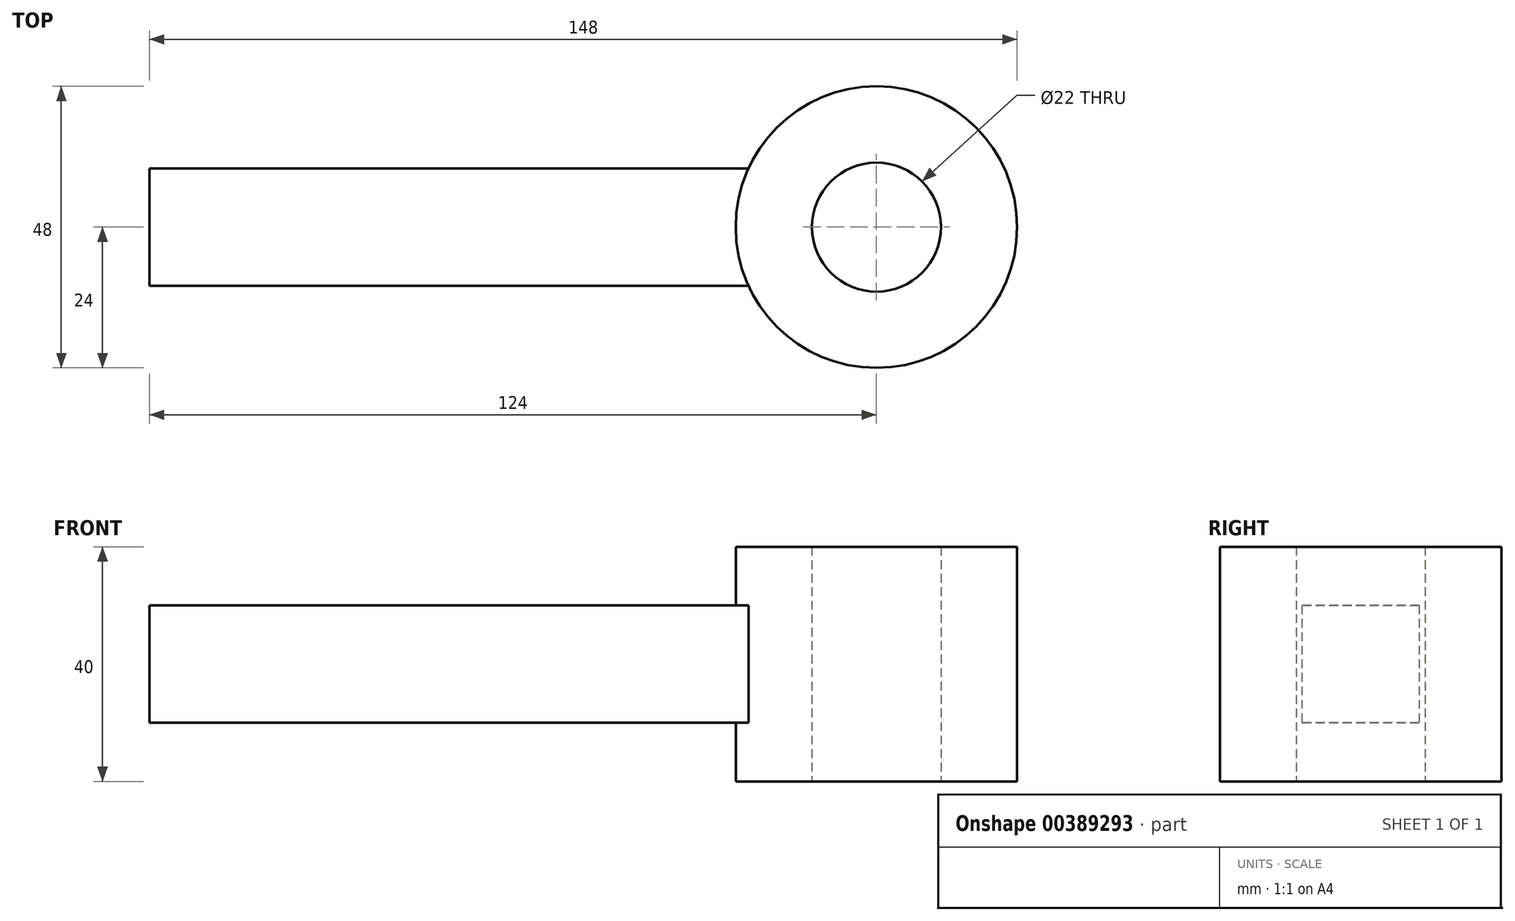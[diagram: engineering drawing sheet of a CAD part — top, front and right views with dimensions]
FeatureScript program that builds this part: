
annotation { "Feature Type Name" : "Feature", "Feature Type Description" : "" }
export const myFeature = defineFeature(function(context is Context, id is Id, definition is map)
    precondition{}
    {
        {
            var Q0;
            Q0=qCreatedBy(makeId("Top.planeOp"),FACE);
            var sketch = newSketch(context, id + "F0", { "sketchPlane" : qUnion([Q0])});
            skCircle(sketch, "E0", {"center": v(0, 0) * mm, "radius": 24 * mm});
            skLineSegment(sketch, "E1", {"start": v(-124, 0) * mm, "end": v(-124, -10) * mm});
            skLineSegment(sketch, "E2", {"start": v(-124, 0) * mm, "end": v(-124, 10) * mm});
            skLineSegment(sketch, "E3", {"start": v(-124, 10) * mm, "end": v(-21.82, 10) * mm});
            skLineSegment(sketch, "E4", {"start": v(-124, -10) * mm, "end": v(-21.82, -10) * mm});
            skCircle(sketch, "E5", {"center": v(0, 0) * mm, "radius": 11 * mm});
            skSolve(sketch);
        }
        {
            var Q0;
            {var subQ0=sQuery(id+"F0.wireOp",EDGE,"E0");var subQ1=makeQuery(id+"F0.imprint","INTERSECT",VERTEX,{"derivedFrom":[subQ0,sQuery(id+"F0.wireOp",EDGE,"E3")]});Q0=makeQuery(id+"F0.imprint","IMPRINT",FACE,{"disambiguationData":[TD([[makeQuery(id+"F0.imprint","IMPRINT",EDGE,{"disambiguationData":[TD([[subQ1,-1.0]])],"derivedFrom":subQ0}),1.0]])]});}
            extrude(context, id + "F1", {"entities" : qUnion([Q0]), "endBound" : BoundingType.SYMMETRIC, "depth" : 40 * mm});
        }
        {
            var Q0;
            Q0=makeQuery(id+"F0.imprint","IMPRINT",FACE,{"disambiguationData":[TD([[makeQuery(id+"F0.imprint","IMPRINT",EDGE,{"derivedFrom":sQuery(id+"F0.wireOp",EDGE,"E1")}),1.0]])]});
            extrude(context, id + "F2", {"entities" : qUnion([Q0]), "operationType" : NewBodyOperationType.ADD, "endBound" : BoundingType.SYMMETRIC, "depth" : 20 * mm});
        }
        {
            var Q0;
            Q0=makeQuery(id+"F0.imprint","IMPRINT",FACE,{"disambiguationData":[TD([[makeQuery(id+"F0.imprint","IMPRINT",EDGE,{"derivedFrom":sQuery(id+"F0.wireOp",EDGE,"E5")}),1.0]])]});
            extrude(context, id + "F3", {"entities" : qUnion([Q0]), "operationType" : NewBodyOperationType.REMOVE, "depth" : 25 * mm});
        }
    });
